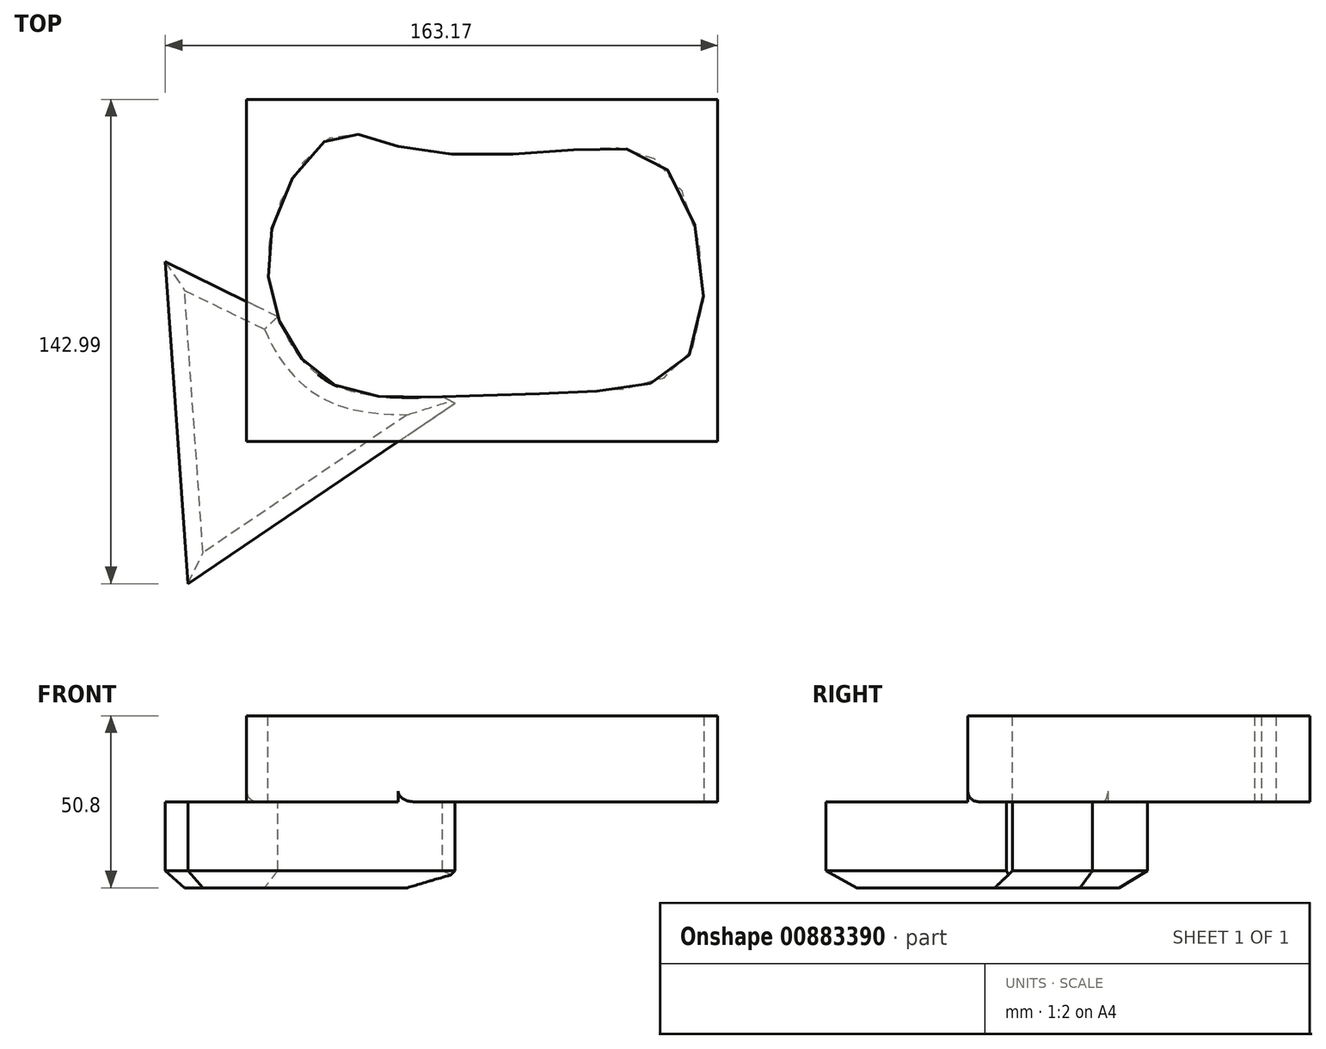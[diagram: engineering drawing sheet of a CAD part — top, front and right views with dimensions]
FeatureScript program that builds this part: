
annotation { "Feature Type Name" : "Feature", "Feature Type Description" : "" }
export const myFeature = defineFeature(function(context is Context, id is Id, definition is map)
    precondition{}
    {
        {
            var Q0;
            Q0=qCreatedBy(makeId("Top.planeOp"),FACE);
            var sketch = newSketch(context, id + "F0", { "sketchPlane" : qUnion([Q0])});
            skLineSegment(sketch, "E0.bottom", {"start": v(69.56, -50.52) * mm, "end": v(-69.56, -50.52) * mm});
            skLineSegment(sketch, "E0.top", {"start": v(69.56, 50.52) * mm, "end": v(-69.56, 50.52) * mm});
            skLineSegment(sketch, "E0.left", {"start": v(69.56, -50.52) * mm, "end": v(69.56, 50.52) * mm});
            skLineSegment(sketch, "E0.right", {"start": v(-69.56, -50.52) * mm, "end": v(-69.56, 50.52) * mm});
            skPoint(sketch, "E0.middle", {"position": v(0, 0) * mm});
            skFitSpline(sketch, "E1", {"points": [v(-43.48, -33.9) * mm, v(-12.59, -37.34) * mm, v(30.3, -35.83) * mm, v(61.7, -24.07) * mm, v(55.3, 29.22) * mm, v(23.58, 35.34) * mm, v(-23.54, 36.3) * mm, v(-43.51, 39.78) * mm, v(-61.84, 13.75) * mm, v(-59.5, -15.7) * mm, v(-43.48, -33.9) * mm]});
            skSolve(sketch);
        }
        {
            var Q0;
            Q0=makeQuery(id+"F0.imprint","IMPRINT",FACE,{"disambiguationData":[TD([[makeQuery(id+"F0.imprint","IMPRINT",EDGE,{"derivedFrom":sQuery(id+"F0.wireOp",EDGE,"E0.bottom")}),-1.0]])]});
            extrude(context, id + "F1", {"entities" : qUnion([Q0]), "depth" : 25.4 * mm, "offsetDistance" : 25.4 * mm});
        }
        {
            var Q0;
            Q0=makeQuery(id+"F1.opExtrude","CAP_FACE",FACE,{"disambiguationData":[OSD([sQuery(id+"F0.wireOp",EDGE,"E0.bottom"),sQuery(id+"F0.wireOp",EDGE,"E0.top"),sQuery(id+"F0.wireOp",EDGE,"E0.left"),sQuery(id+"F0.wireOp",EDGE,"E0.right"),sQuery(id+"F0.wireOp",EDGE,"E1")])],"isStart":true});
            var sketch = newSketch(context, id + "F2", { "sketchPlane" : qUnion([Q0])});
            skCircle(sketch, "E2.cCircle", {"center": v(-62.82, 43.03) * mm, "radius": 27.5 * mm, "construction": true});
            skLineSegment(sketch, "E2.0", {"start": v(-7.97, 39.16) * mm, "end": v(-93.6, -2.54) * mm});
            skLineSegment(sketch, "E2.1", {"start": v(-93.6, -2.54) * mm, "end": v(-86.9, 92.47) * mm});
            skLineSegment(sketch, "E2.2", {"start": v(-86.9, 92.47) * mm, "end": v(-7.97, 39.16) * mm});
            skPoint(sketch, "E2.0.midPoint", {"position": v(-50.79, 18.3) * mm});
            skSolve(sketch);
        }
        {
            var Q0;
            {var subQ5=sQuery(id+"F2.wireOp",EDGE,"E2.1");Q0=makeQuery(id+"F2.imprint","IMPRINT",FACE,{"disambiguationData":[TD([[makeQuery(id+"F2.imprint","IMPRINT",EDGE,{"derivedFrom":subQ5}),-1.0]])]});}
            var Q1;
            {var subQ0=sQuery(id+"F2.wireOp",EDGE,"E2.2");var subQ1=sQuery(id+"F2.wireOp",EDGE,"E2.0");var subQ2=makeQuery(id+"F2.imprint","INTERSECT",VERTEX,{"derivedFrom":[subQ1,subQ0]});Q1=makeQuery(id+"F2.imprint","IMPRINT",FACE,{"disambiguationData":[TD([[makeQuery(id+"F2.imprint","IMPRINT",EDGE,{"disambiguationData":[TD([[subQ2,-1.0]])],"derivedFrom":subQ1}),-1.0]])]});}
            extrude(context, id + "F3", {"entities" : qUnion([Q0, Q1]), "operationType" : NewBodyOperationType.ADD, "depth" : 25.4 * mm, "offsetDistance" : 25.4 * mm});
        }
        {
            var Q0;
            {var subQ0=sQuery(id+"F0.wireOp",EDGE,"E0.bottom");Q0=makeQuery(id+"F3.boolean.opBoolean","SPLIT",EDGE,{"disambiguationData":[topologyDisambiguationEdgeConnected([makeQuery(id+"F3.opExtrude","CAP_FACE",FACE,{"disambiguationData":[OSD([sQuery(id+"F0.wireOp",EDGE,"E1"),sQuery(id+"F2.wireOp",EDGE,"E2.0"),sQuery(id+"F2.wireOp",EDGE,"E2.1"),sQuery(id+"F2.wireOp",EDGE,"E2.2")])],"isStart":true})])],"derivedFrom":makeQuery(id+"F1.opExtrude","CAP_EDGE",EDGE,{"disambiguationData":[OSD([subQ0])],"isStart":true})});}
            var Q1;
            {var subQ0=sQuery(id+"F0.wireOp",EDGE,"E0.right");Q1=makeQuery(id+"F3.boolean.opBoolean","SPLIT",EDGE,{"disambiguationData":[topologyDisambiguationEdgeConnected([makeQuery(id+"F3.opExtrude","CAP_FACE",FACE,{"disambiguationData":[OSD([sQuery(id+"F0.wireOp",EDGE,"E1"),sQuery(id+"F2.wireOp",EDGE,"E2.0"),sQuery(id+"F2.wireOp",EDGE,"E2.1"),sQuery(id+"F2.wireOp",EDGE,"E2.2")])],"isStart":true})])],"derivedFrom":makeQuery(id+"F1.opExtrude","CAP_EDGE",EDGE,{"disambiguationData":[OSD([subQ0])],"isStart":true})});}
            fillet(context, id + "F4", {"entities" : qUnion([Q0, Q1]), "radius" : 3.17 * mm, "tangentPropagation" : true, "allowEdgeOverflow" : false});
        }
        {
            var Q0;
            Q0=makeQuery(id+"F3.opExtrude","CAP_EDGE",EDGE,{"disambiguationData":[OSD([sQuery(id+"F2.wireOp",EDGE,"E2.1")])],"isStart":false});
            var Q1;
            Q1=makeQuery(id+"F3.opExtrude","CAP_EDGE",EDGE,{"disambiguationData":[OSD([sQuery(id+"F2.wireOp",EDGE,"E2.2")])],"isStart":false});
            var Q2;
            Q2=makeQuery(id+"F3.opExtrude","CAP_EDGE",EDGE,{"disambiguationData":[OSD([sQuery(id+"F0.wireOp",EDGE,"E1")])],"isStart":false});
            var Q3;
            {var subQ0=sQuery(id+"F2.wireOp",EDGE,"E2.0");var subQ1=makeQuery(id+"F2.imprint","INTERSECT",VERTEX,{"derivedFrom":[makeQuery(id+"F1.opExtrude","CAP_EDGE",EDGE,{"disambiguationData":[OSD([sQuery(id+"F0.wireOp",EDGE,"E0.right")])],"isStart":true}),subQ0]});Q3=makeQuery(id+"F3.opExtrude","CAP_EDGE",EDGE,{"disambiguationData":[OSD([subQ0]),TDD([makeQuery(id+"F2.imprint","IMPRINT",EDGE,{"disambiguationData":[TD([[subQ1,1.0]])],"derivedFrom":subQ0}),makeQuery(id+"F2.imprint","IMPRINT",EDGE,{"disambiguationData":[TD([[makeQuery(id+"F2.imprint","INTERSECT",VERTEX,{"derivedFrom":[subQ0,sQuery(id+"F2.wireOp",EDGE,"E2.1")]}),1.0]])],"derivedFrom":subQ0})])],"isStart":false});}
            var Q4;
            {var subQ0=sQuery(id+"F2.wireOp",EDGE,"E2.0");Q4=makeQuery(id+"F3.opExtrude","CAP_EDGE",EDGE,{"disambiguationData":[OSD([subQ0]),TDD([makeQuery(id+"F2.imprint","IMPRINT",EDGE,{"disambiguationData":[TD([[makeQuery(id+"F2.imprint","INTERSECT",VERTEX,{"derivedFrom":[subQ0,sQuery(id+"F2.wireOp",EDGE,"E2.2")]}),-1.0]])],"derivedFrom":subQ0})])],"isStart":false});}
            chamfer(context, id + "F5", {"entities" : qUnion([Q0, Q1, Q2, Q3, Q4]), "width" : 5.08 * mm, "tangentPropagation" : true});
        }
        {
            var Q0;
            Q0=qCreatedBy(makeId("Right.planeOp"),FACE);
            var sketch = newSketch(context, id + "F6", { "sketchPlane" : qUnion([Q0])});
            skCircle(sketch, "E3", {"center": v(-75.15, 36.52) * mm, "radius": 30.76 * mm});
            skSolve(sketch);
        }
        {
            var Q0;
            Q0=sQuery(id+"F6.wireOp",EDGE,"E3");
            extrude(context, id + "F7", {"bodyType" : ToolBodyType.SURFACE, "surfaceEntities" : qUnion([Q0]), "depth" : 25.4 * mm, "offsetDistance" : 25.4 * mm});
        }
    });
